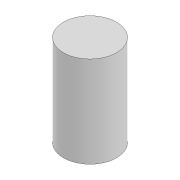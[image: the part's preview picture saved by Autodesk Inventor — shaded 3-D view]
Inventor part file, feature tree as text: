
AUTODESK INVENTOR PART (.ipt)
format: ipt  version: 2022 (Build 260153000, 153)  size: 93,184 bytes
history: native  units: mm
features: extrude x2, sketch x2
ambient origin geometry x8: Origin, YZ Plane, XZ Plane, XY Plane, X Axis, Y Axis, Z Axis, Center Point
bodies: Solid1 (feature_tree)
feature tree (4):
  extrude  "Extrusion1"  Depth=2.0mm
  extrude  "Extrusion2"  Depth=4.0mm TaperAngle=0.0deg
  sketch  "Sketch1"  dims[d0=4.15mm d1=2.0mm]
  sketch  "Sketch2"  dims[d2=10.0mm d3=0.0mm d4=4.0mm d5=0.0mm]
